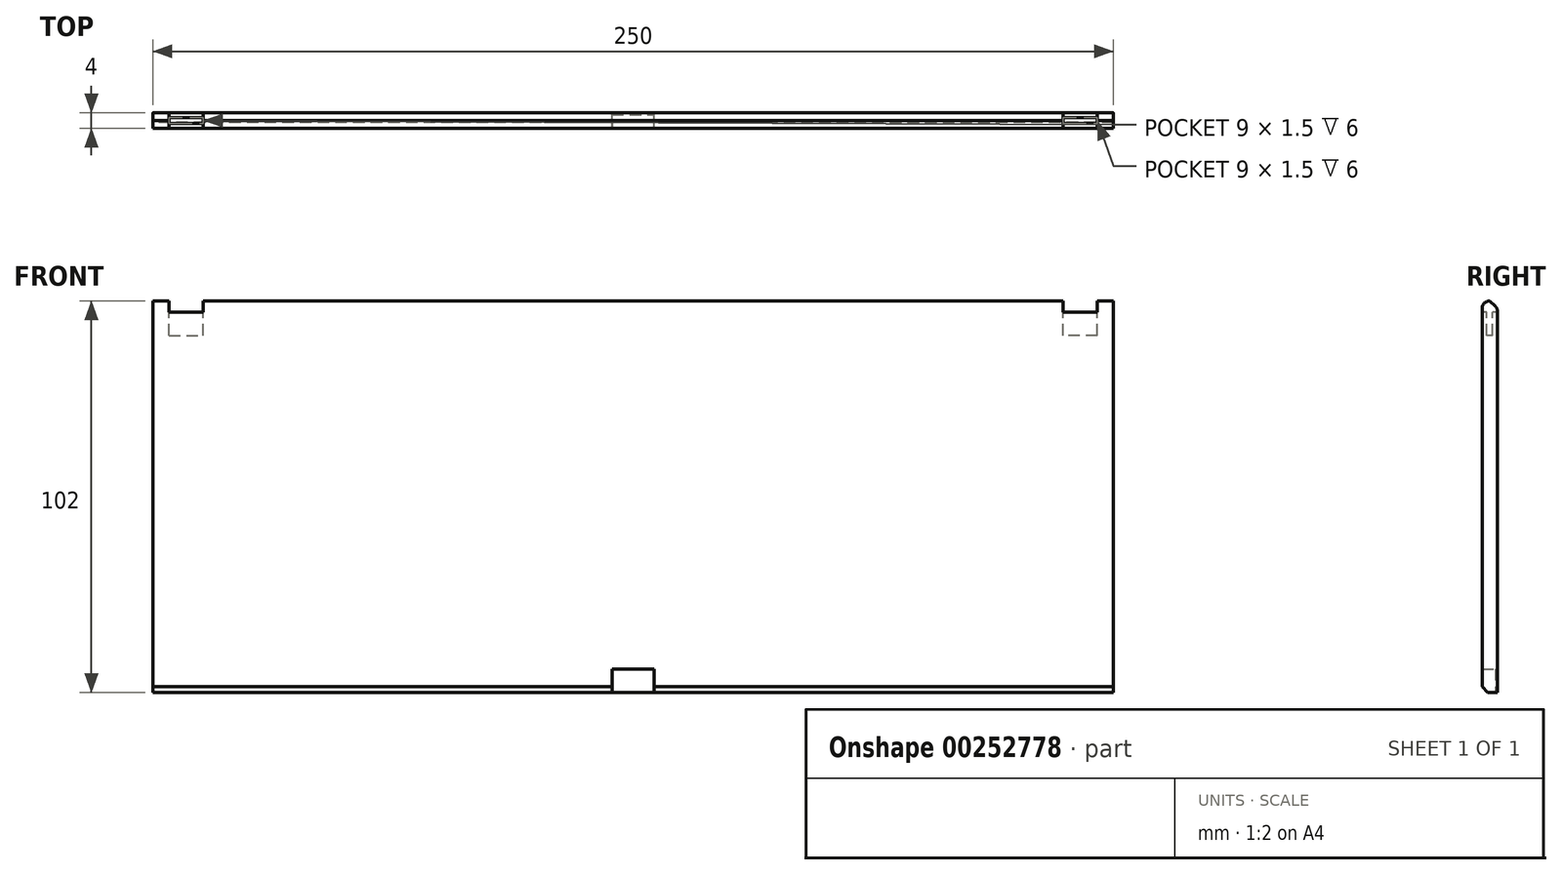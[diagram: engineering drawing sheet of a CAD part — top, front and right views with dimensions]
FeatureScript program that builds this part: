
annotation { "Feature Type Name" : "Feature", "Feature Type Description" : "" }
export const myFeature = defineFeature(function(context is Context, id is Id, definition is map)
    precondition{}
    {
        {
            var Q0;
            Q0=qCreatedBy(makeId("Front.planeOp"),FACE);
            var sketch = newSketch(context, id + "F0", { "sketchPlane" : qUnion([Q0])});
            skLineSegment(sketch, "E0.bottom", {"start": v(125, 50) * mm, "end": v(-125, 50) * mm});
            skLineSegment(sketch, "E0.top", {"start": v(125, -50) * mm, "end": v(-125, -50) * mm});
            skLineSegment(sketch, "E0.left", {"start": v(125, 50) * mm, "end": v(125, -50) * mm});
            skLineSegment(sketch, "E0.right", {"start": v(-125, 50) * mm, "end": v(-125, -50) * mm});
            skPoint(sketch, "E0.middle", {"position": v(0, 0) * mm});
            skSolve(sketch);
        }
        {
            var Q0;
            Q0=makeQuery(id+"F0.imprint","IMPRINT",FACE,{"disambiguationData":[TD([[makeQuery(id+"F0.imprint","IMPRINT",EDGE,{"derivedFrom":sQuery(id+"F0.wireOp",EDGE,"E0.bottom")}),1.0]])]});
            extrude(context, id + "F1", {"entities" : qUnion([Q0]), "endBound" : BoundingType.SYMMETRIC, "depth" : 4 * mm});
        }
        {
            var Q0;
            Q0=makeQuery(id+"F1.opExtrude","SWEPT_FACE",FACE,{"disambiguationData":[OSD([sQuery(id+"F0.wireOp",EDGE,"E0.left")])]});
            var sketch = newSketch(context, id + "F2", { "sketchPlane" : qUnion([Q0])});
            skArc(sketch, "E1", {"start": v(0, 52) * mm, "mid": v(-1.4, 48.57) * mm, "end": v(2, 50.05) * mm});
            skLineSegment(sketch, "E2", {"start": v(0, 52) * mm, "end": v(2, 50.05) * mm});
            skCircle(sketch, "E3", {"center": v(0, -50) * mm, "radius": 2 * mm});
            skSolve(sketch);
        }
        {
            var Q0;
            Q0=makeQuery(id+"F1.opExtrude","SWEPT_FACE",FACE,{"disambiguationData":[OSD([sQuery(id+"F0.wireOp",EDGE,"E0.bottom")])]});
            var sketch = newSketch(context, id + "F3", { "sketchPlane" : qUnion([Q0])});
            skPoint(sketch, "E4.middle", {"position": v(0, -2) * mm});
            skLineSegment(sketch, "E5.bottom", {"start": v(-111.83, 2.1) * mm, "end": v(-120.83, 2.1) * mm});
            skLineSegment(sketch, "E5.top", {"start": v(-111.83, -2.1) * mm, "end": v(-120.83, -2.1) * mm});
            skLineSegment(sketch, "E5.left", {"start": v(-111.83, 2.1) * mm, "end": v(-111.83, -2.1) * mm});
            skLineSegment(sketch, "E5.right", {"start": v(-120.83, 2.1) * mm, "end": v(-120.83, -2.1) * mm});
            skPoint(sketch, "E5.middle", {"position": v(0, 0) * mm});
            skLineSegment(sketch, "E6.MirrorCS", {"start": v(120.83, 2.1) * mm, "end": v(120.83, -2.1) * mm});
            skLineSegment(sketch, "E7.MirrorCS", {"start": v(111.83, 2.1) * mm, "end": v(120.83, 2.1) * mm});
            skLineSegment(sketch, "E8.MirrorCS", {"start": v(111.83, -2.1) * mm, "end": v(120.83, -2.1) * mm});
            skLineSegment(sketch, "E9.MirrorCS", {"start": v(111.83, 2.1) * mm, "end": v(111.83, -2.1) * mm});
            skSolve(sketch);
        }
        {
            var Q0;
            {var subQ3=sQuery(id+"F2.wireOp",EDGE,"E2");Q0=makeQuery(id+"F2.imprint","IMPRINT",FACE,{"disambiguationData":[TD([[makeQuery(id+"F2.imprint","IMPRINT",EDGE,{"derivedFrom":subQ3}),-1.0]])]});}
            extrude(context, id + "F4", {"entities" : qUnion([Q0]), "operationType" : NewBodyOperationType.ADD, "oppositeDirection" : true, "depth" : 250 * mm});
        }
        {
            var Q0;
            {var subQ0=sQuery(id+"F2.wireOp",EDGE,"E2");var subQ1=sQuery(id+"F2.wireOp",EDGE,"E1");Q0=makeQuery(id+"F4.opExtrude","SWEPT_EDGE",EDGE,{"disambiguationData":[OSD([subQ1,subQ0]),TDD([makeQuery(id+"F2.imprint","INTERSECT",VERTEX,{"disambiguationData":[OD(1.0)],"derivedFrom":[subQ1,subQ0]})])]});}
            fillet(context, id + "F5", {"entities" : qUnion([Q0]), "radius" : 1.7 * mm, "tangentPropagation" : true, "allowEdgeOverflow" : false});
        }
        {
            var Q0;
            Q0=makeQuery(id+"F1.opExtrude","SWEPT_BODY",BODY,{"disambiguationData":[OSD([sQuery(id+"F0.wireOp",EDGE,"E0.bottom"),sQuery(id+"F0.wireOp",EDGE,"E0.top"),sQuery(id+"F0.wireOp",EDGE,"E0.left"),sQuery(id+"F0.wireOp",EDGE,"E0.right")])]});
            transform(context, id + "F6", {"entities" : qUnion([Q0]), "transformType" : TransformType.COPY});
        }
        {
            var Q0;
            Q0=makeQuery(id+"F6.opPattern","COPY",BODY,{"derivedFrom":makeQuery(id+"F1.opExtrude","SWEPT_BODY",BODY,{"disambiguationData":[OSD([sQuery(id+"F0.wireOp",EDGE,"E0.bottom"),sQuery(id+"F0.wireOp",EDGE,"E0.top"),sQuery(id+"F0.wireOp",EDGE,"E0.left"),sQuery(id+"F0.wireOp",EDGE,"E0.right")])]}),"instanceName":"1"});
            deleteBodies(context, id + "F7", {"entities" : qUnion([Q0])});
        }
        {
            var Q0;
            Q0 = qSketchRegion(id + "F3", true);
            extrude(context, id + "F8", {"entities" : qUnion([Q0]), "operationType" : NewBodyOperationType.REMOVE, "oppositeDirection" : true, "depth" : 1 * mm});
        }
        {
            var Q0;
            Q0=makeQuery(id+"F8.boolean.opBoolean","COPY",FACE,{"derivedFrom":makeQuery(id+"F8.opExtrude","CAP_FACE",FACE,{"disambiguationData":[OSD([sQuery(id+"F3.wireOp",EDGE,"E5.bottom"),sQuery(id+"F3.wireOp",EDGE,"E5.top"),sQuery(id+"F3.wireOp",EDGE,"E5.left"),sQuery(id+"F3.wireOp",EDGE,"E5.right")])],"isStart":false})});
            var sketch = newSketch(context, id + "F9", { "sketchPlane" : qUnion([Q0])});
            skLineSegment(sketch, "E10.bottom", {"start": v(-120.83, 0.75) * mm, "end": v(-111.83, 0.75) * mm});
            skLineSegment(sketch, "E10.top", {"start": v(-120.83, -0.75) * mm, "end": v(-111.83, -0.75) * mm});
            skLineSegment(sketch, "E10.left", {"start": v(-120.83, 0.75) * mm, "end": v(-120.83, -0.75) * mm});
            skLineSegment(sketch, "E10.right", {"start": v(-111.83, 0.75) * mm, "end": v(-111.83, -0.75) * mm});
            skPoint(sketch, "E10.middle", {"position": v(0, 0) * mm});
            skLineSegment(sketch, "E11.MirrorCS", {"start": v(120.83, 0.75) * mm, "end": v(120.83, -0.75) * mm});
            skLineSegment(sketch, "E12.MirrorCS", {"start": v(120.83, -0.75) * mm, "end": v(111.83, -0.75) * mm});
            skLineSegment(sketch, "E13.MirrorCS", {"start": v(120.83, 0.75) * mm, "end": v(111.83, 0.75) * mm});
            skLineSegment(sketch, "E14.MirrorCS", {"start": v(111.83, 0.75) * mm, "end": v(111.83, -0.75) * mm});
            skSolve(sketch);
        }
        {
            var Q0;
            Q0=makeQuery(id+"F9.imprint","IMPRINT",FACE,{"disambiguationData":[TD([[makeQuery(id+"F9.imprint","IMPRINT",EDGE,{"derivedFrom":sQuery(id+"F9.wireOp",EDGE,"E10.bottom")}),-1.0]])]});
            extrude(context, id + "F10", {"entities" : qUnion([Q0]), "operationType" : NewBodyOperationType.REMOVE, "oppositeDirection" : true, "depth" : 6 * mm});
        }
        {
            var Q0;
            Q0 = qSketchRegion(id + "F3", true);
            extrude(context, id + "F11", {"entities" : qUnion([Q0]), "operationType" : NewBodyOperationType.REMOVE, "depth" : 25.4 * mm});
        }
        {
            var Q0;
            Q0 = qSketchRegion(id + "F9", true);
            extrude(context, id + "F12", {"entities" : qUnion([Q0]), "operationType" : NewBodyOperationType.REMOVE, "oppositeDirection" : true, "depth" : 6 * mm});
        }
        {
            var Q0;
            Q0=makeQuery(id+"F1.opExtrude","SWEPT_FACE",FACE,{"disambiguationData":[OSD([sQuery(id+"F0.wireOp",EDGE,"E0.top")])]});
            var sketch = newSketch(context, id + "F13", { "sketchPlane" : qUnion([Q0])});
            skLineSegment(sketch, "E15.bottom", {"start": v(-5.5, 2) * mm, "end": v(5.5, 2) * mm});
            skLineSegment(sketch, "E15.top", {"start": v(-5.5, -1.5) * mm, "end": v(5.5, -1.5) * mm});
            skLineSegment(sketch, "E15.left", {"start": v(-5.5, 2) * mm, "end": v(-5.5, -1.5) * mm});
            skLineSegment(sketch, "E15.right", {"start": v(5.5, 2) * mm, "end": v(5.5, -1.5) * mm});
            skPoint(sketch, "E15.middle", {"position": v(0, 0) * mm});
            skSolve(sketch);
        }
        {
            var Q0;
            Q0=makeQuery(id+"F13.imprint","IMPRINT",FACE,{"disambiguationData":[TD([[makeQuery(id+"F13.imprint","IMPRINT",EDGE,{"derivedFrom":sQuery(id+"F13.wireOp",EDGE,"E15.bottom")}),1.0]])]});
            extrude(context, id + "F14", {"entities" : qUnion([Q0]), "operationType" : NewBodyOperationType.REMOVE, "oppositeDirection" : true, "depth" : 6.12 * mm});
        }
        {
            var Q0;
            {var subQ0=sQuery(id+"F0.wireOp",EDGE,"E0.left");var subQ2=sQuery(id+"F0.wireOp",EDGE,"E0.top");Q0=makeQuery(id+"F14.boolean.opBoolean","SPLIT",EDGE,{"disambiguationData":[TD([makeQuery(id+"F1.opExtrude","SWEPT_FACE",FACE,{"disambiguationData":[OSD([subQ0])]})])],"derivedFrom":makeQuery(id+"F1.opExtrude","CAP_EDGE",EDGE,{"disambiguationData":[OSD([subQ2])],"isStart":false})});}
            var Q1;
            {var subQ0=sQuery(id+"F0.wireOp",EDGE,"E0.right");var subQ1=sQuery(id+"F0.wireOp",EDGE,"E0.top");Q1=makeQuery(id+"F14.boolean.opBoolean","SPLIT",EDGE,{"disambiguationData":[TD([makeQuery(id+"F1.opExtrude","SWEPT_FACE",FACE,{"disambiguationData":[OSD([subQ0])]})])],"derivedFrom":makeQuery(id+"F1.opExtrude","CAP_EDGE",EDGE,{"disambiguationData":[OSD([subQ1])],"isStart":false})});}
            chamfer(context, id + "F15", {"entities" : qUnion([Q0, Q1]), "width" : 1.5 * mm, "tangentPropagation" : true});
        }
    });
